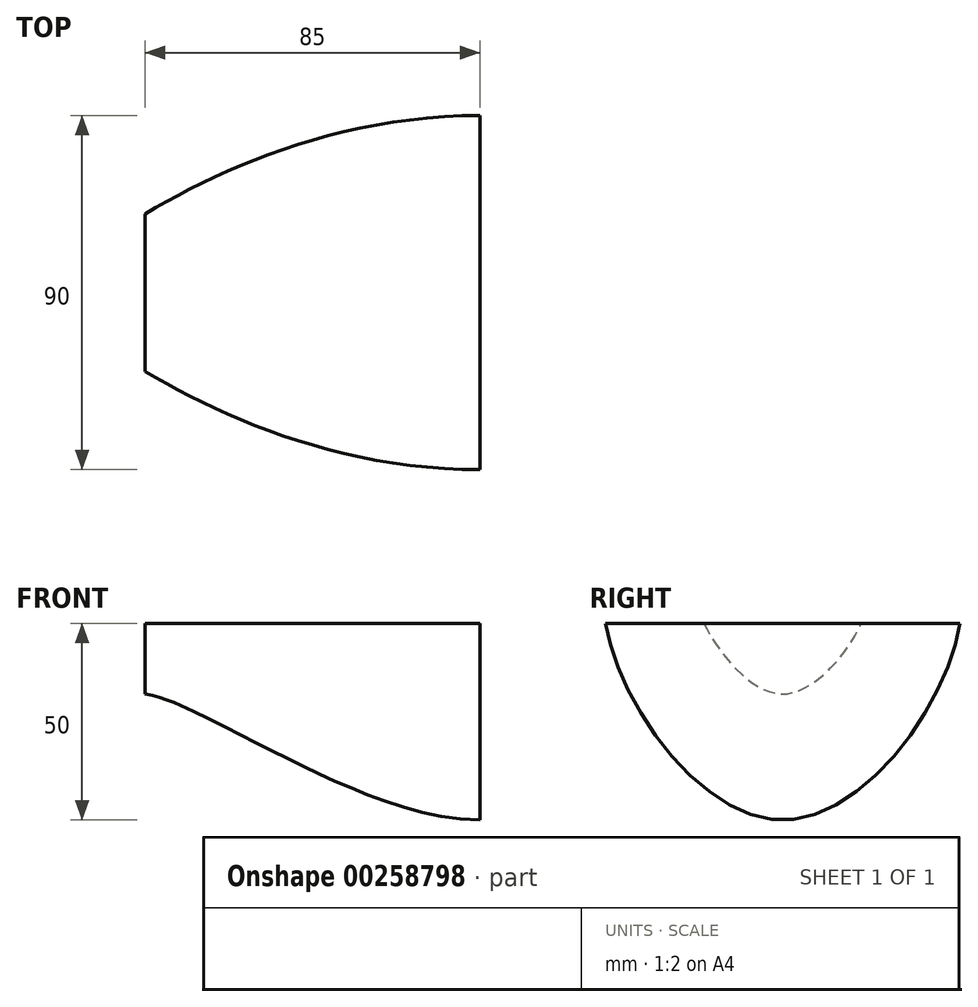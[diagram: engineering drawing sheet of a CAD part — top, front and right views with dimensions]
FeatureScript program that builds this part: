
annotation { "Feature Type Name" : "Feature", "Feature Type Description" : "" }
export const myFeature = defineFeature(function(context is Context, id is Id, definition is map)
    precondition{}
    {
        {
            var Q0;
            Q0=qCreatedBy(makeId("Right.planeOp"),FACE);
            var sketch = newSketch(context, id + "F0", { "sketchPlane" : qUnion([Q0])});
            skFitSpline(sketch, "E0", {"points": [v(-45, 0) * mm, v(0, -50) * mm, v(45, 0) * mm], "startDerivative": vector(18, -120) * mm, "endDerivative": vector(18, 120) * mm});
            skLineSegment(sketch, "E1", {"start": v(-45, 0) * mm, "end": v(45, 0) * mm});
            skSolve(sketch);
        }
        {
            var Q0;
            Q0=qCreatedBy(makeId("Right.planeOp"),FACE);
            cPlane(context, id + "F1", {"entities" : qUnion([Q0]), "cplaneType" : CPlaneType.OFFSET, "offset" : 85 * mm, "oppositeDirection" : true, "width" : 150 * mm, "height" : 150 * mm});
        }
        {
            var Q0;
            Q0=qCreatedBy(id+"F1.planeOp",FACE);
            var sketch = newSketch(context, id + "F2", { "sketchPlane" : qUnion([Q0])});
            skFitSpline(sketch, "E2", {"points": [v(-20, 0) * mm, v(0, -18) * mm, v(20, 0) * mm], "startDerivative": vector(12, -30) * mm, "endDerivative": vector(12, 30) * mm});
            skLineSegment(sketch, "E3", {"start": v(-20, 0) * mm, "end": v(20, 0) * mm});
            skSolve(sketch);
        }
        {
            var Q0;
            Q0=qCreatedBy(makeId("Top.planeOp"),FACE);
            var sketch = newSketch(context, id + "F3", { "sketchPlane" : qUnion([Q0])});
            skPoint(sketch, "E4.0", {"position": v(-85, 20) * mm});
            skPoint(sketch, "E5.0", {"position": v(0, 45) * mm});
            skFitSpline(sketch, "E6", {"points": [v(-85, 20) * mm, v(0, 45) * mm], "startDerivative": vector(60, 36) * mm, "endDerivative": vector(105, 0) * mm});
            skPoint(sketch, "E7.0", {"position": v(-85, -20) * mm});
            skPoint(sketch, "E8.0", {"position": v(0, -45) * mm});
            skFitSpline(sketch, "E9", {"points": [v(-85, -20) * mm, v(0, -45) * mm], "startDerivative": vector(60, -36) * mm, "endDerivative": vector(105, 0) * mm});
            skLineSegment(sketch, "E10", {"start": v(0, 45) * mm, "end": v(0, -45) * mm});
            skSolve(sketch);
        }
        {
            var Q0;
            Q0=qCreatedBy(makeId("Front.planeOp"),FACE);
            var sketch = newSketch(context, id + "F4", { "sketchPlane" : qUnion([Q0])});
            skPoint(sketch, "E11.0", {"position": v(-85, -18) * mm});
            skPoint(sketch, "E12.0", {"position": v(0, -50) * mm});
            skFitSpline(sketch, "E13", {"points": [v(-85, -18) * mm, v(0, -50) * mm], "startDerivative": vector(45, -6) * mm, "endDerivative": vector(89.92, 0) * mm});
            skSolve(sketch);
        }
        {
            var Q0;
            Q0=makeQuery(id+"F0.imprint","IMPRINT",FACE,{"disambiguationData":[TD([[makeQuery(id+"F0.imprint","IMPRINT",EDGE,{"derivedFrom":sQuery(id+"F0.wireOp",EDGE,"E0")}),1.0]])]});
            var Q1;
            Q1=makeQuery(id+"F2.imprint","IMPRINT",FACE,{"disambiguationData":[TD([[makeQuery(id+"F2.imprint","IMPRINT",EDGE,{"derivedFrom":sQuery(id+"F2.wireOp",EDGE,"E2")}),1.0]])]});
            var Q2;
            Q2=sQuery(id+"F3.wireOp",EDGE,"E6");
            var Q3;
            Q3=sQuery(id+"F3.wireOp",EDGE,"E9");
            var Q4;
            Q4=sQuery(id+"F4.wireOp",EDGE,"E13");
            loft(context, id + "F5", {"addGuides" : true, "sheetProfilesArray" : [{ "sheetProfileEntities" : qUnion([Q0]) }, { "sheetProfileEntities" : qUnion([Q1]) }], "guidesArray" : [{ "guideEntities" : qUnion([Q2]), "guideDerivativeType" : LoftGuideDerivativeType.DEFAULT, "guideDerivativeMagnitude" : 1 }, { "guideEntities" : qUnion([Q3]), "guideDerivativeType" : LoftGuideDerivativeType.DEFAULT, "guideDerivativeMagnitude" : 1 }, { "guideEntities" : qUnion([Q4]), "guideDerivativeType" : LoftGuideDerivativeType.DEFAULT, "guideDerivativeMagnitude" : 1 }]});
        }
    });
